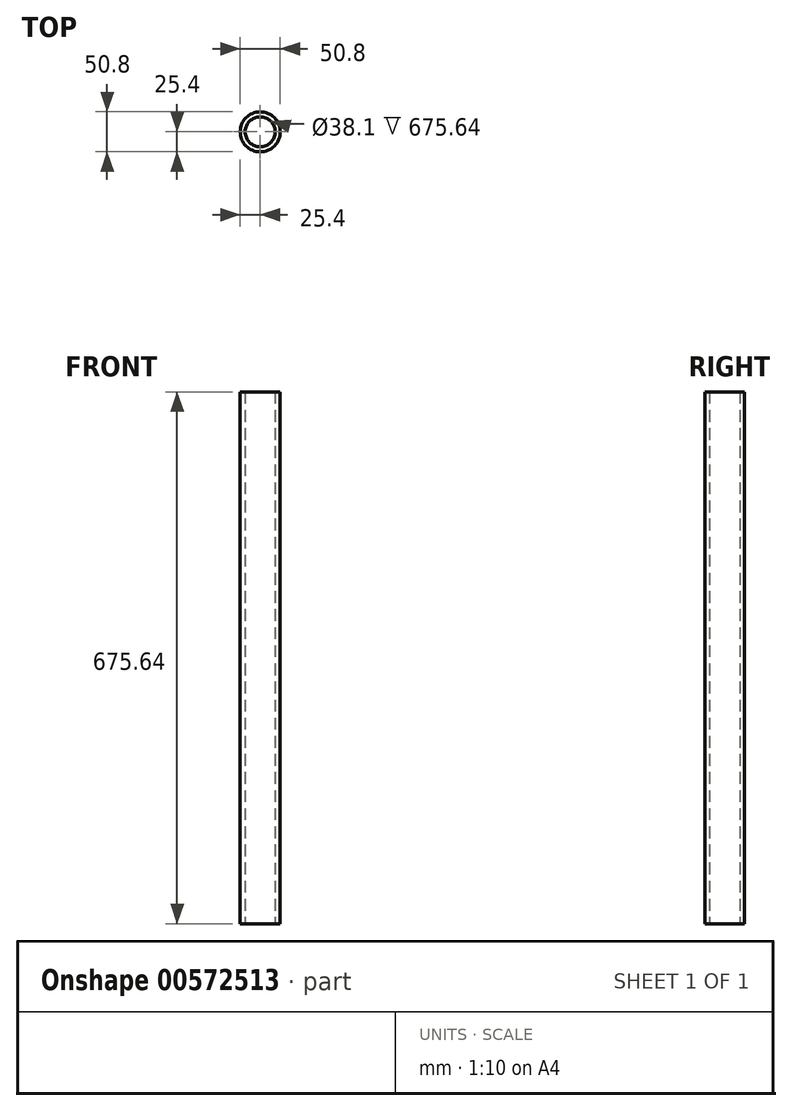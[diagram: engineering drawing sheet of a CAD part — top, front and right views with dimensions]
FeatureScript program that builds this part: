
annotation { "Feature Type Name" : "Feature", "Feature Type Description" : "" }
export const myFeature = defineFeature(function(context is Context, id is Id, definition is map)
    precondition{}
    {
        {
            var Q0;
            Q0=qCreatedBy(makeId("Top.planeOp"),FACE);
            var sketch = newSketch(context, id + "F0", { "sketchPlane" : qUnion([Q0])});
            skCircle(sketch, "E0", {"center": v(0, 0) * mm, "radius": 25.4 * mm});
            skCircle(sketch, "E1", {"center": v(0, 0) * mm, "radius": 19.05 * mm});
            skSolve(sketch);
        }
        {
            var Q0;
            Q0 = qSketchRegion(id + "F0", true);
            extrude(context, id + "F1", {"entities" : qUnion([Q0]), "depth" : 675.64 * mm, "offsetDistance" : 25.4 * mm});
        }
    });
